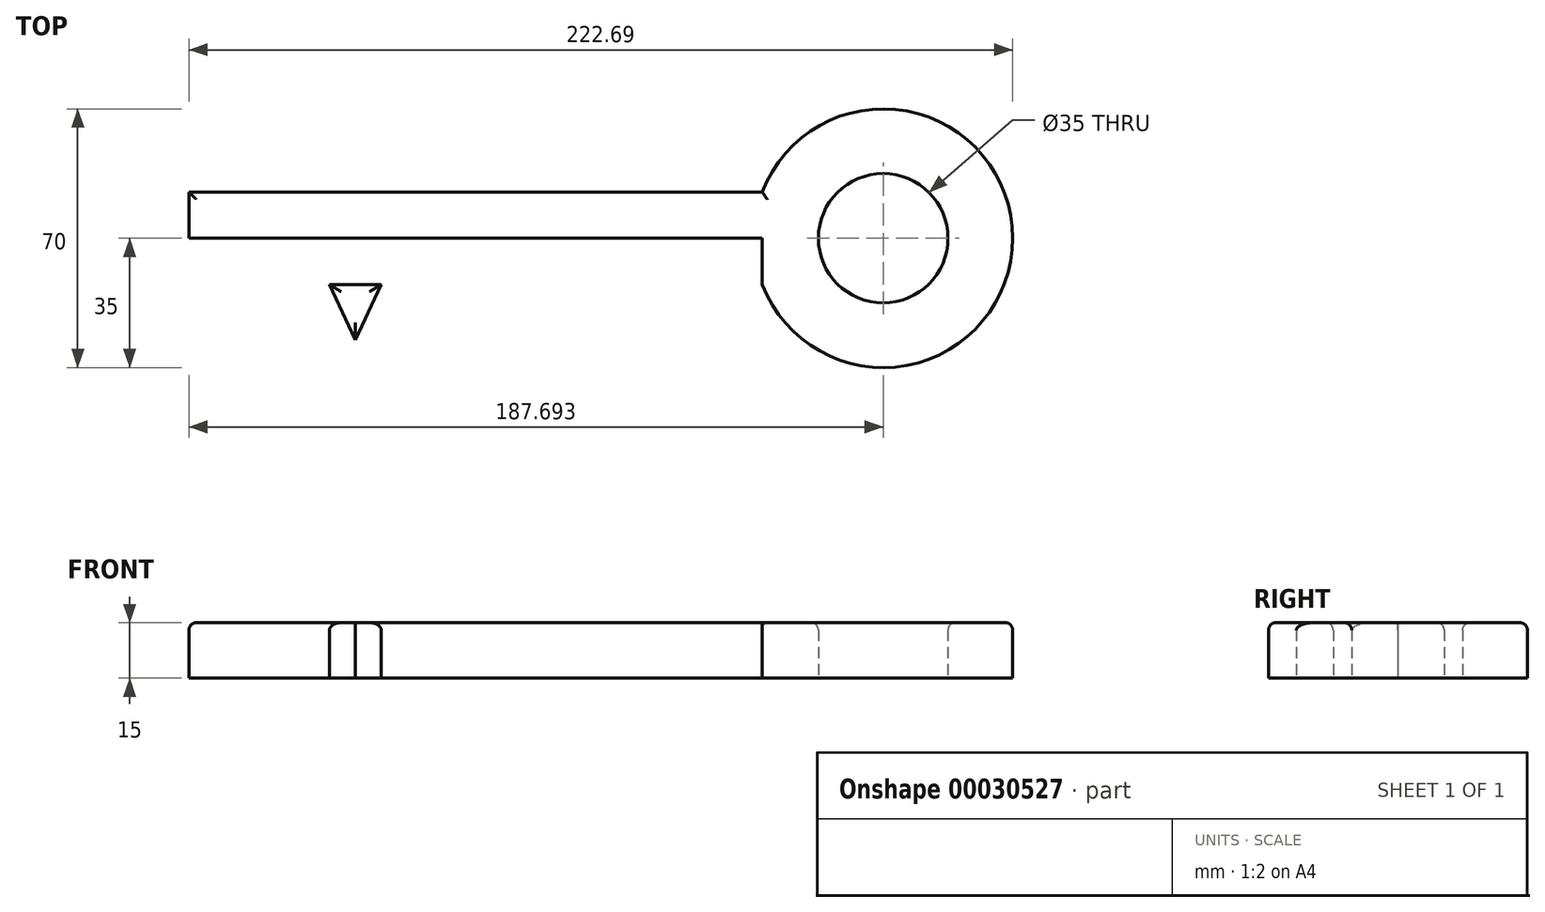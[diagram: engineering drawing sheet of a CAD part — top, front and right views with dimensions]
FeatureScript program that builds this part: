
annotation { "Feature Type Name" : "Feature", "Feature Type Description" : "" }
export const myFeature = defineFeature(function(context is Context, id is Id, definition is map)
    precondition{}
    {
        {
            var Q0;
            Q0=qCreatedBy(makeId("Top.planeOp"),FACE);
            var sketch = newSketch(context, id + "F0", { "sketchPlane" : qUnion([Q0])});
            skLineSegment(sketch, "E0.bottom", {"start": v(-137.39, 40) * mm, "end": v(17.61, 40) * mm});
            skLineSegment(sketch, "E0.top", {"start": v(-137.39, 15) * mm, "end": v(17.61, 15) * mm});
            skLineSegment(sketch, "E0.left", {"start": v(-137.39, 40) * mm, "end": v(-137.39, 15) * mm});
            skLineSegment(sketch, "E0.right", {"start": v(17.61, 40) * mm, "end": v(17.61, 15) * mm});
            skLineSegment(sketch, "E1.bottom", {"start": v(-137.39, 15) * mm, "end": v(-127.39, 15) * mm});
            skLineSegment(sketch, "E1.top", {"start": v(-137.39, -15) * mm, "end": v(-127.39, -15) * mm});
            skLineSegment(sketch, "E1.left", {"start": v(-137.39, 15) * mm, "end": v(-137.39, -15) * mm});
            skLineSegment(sketch, "E1.right", {"start": v(-127.39, 15) * mm, "end": v(-127.39, -15) * mm});
            skLineSegment(sketch, "E2.bottom", {"start": v(-117.39, 15) * mm, "end": v(-109.39, 15) * mm});
            skLineSegment(sketch, "E2.top", {"start": v(-117.39, 0) * mm, "end": v(-109.39, 0) * mm});
            skLineSegment(sketch, "E2.left", {"start": v(-117.39, 15) * mm, "end": v(-117.39, 0) * mm});
            skLineSegment(sketch, "E2.right", {"start": v(-109.39, 15) * mm, "end": v(-109.39, 0) * mm});
            skArc(sketch, "E3", {"start": v(17.61, 15) * mm, "mid": v(85.3, 27.5) * mm, "end": v(17.61, 40) * mm});
            skLineSegment(sketch, "E4", {"start": v(-137.39, 27.5) * mm, "end": v(50.3, 27.5) * mm});
            skLineSegment(sketch, "E5", {"start": v(-99.39, 15) * mm, "end": v(-92.39, 0) * mm});
            skLineSegment(sketch, "E6", {"start": v(-92.39, 0) * mm, "end": v(-85.39, 15) * mm});
            skLineSegment(sketch, "E7", {"start": v(-85.39, 15) * mm, "end": v(-99.39, 15) * mm});
            skCircle(sketch, "E8", {"center": v(50.3, 27.5) * mm, "radius": 17.5 * mm});
            skSolve(sketch);
        }
        {
            var Q0;
            {var subQ5=sQuery(id+"F0.wireOp",EDGE,"E0.bottom");Q0=makeQuery(id+"F0.imprint","IMPRINT",FACE,{"disambiguationData":[TD([[makeQuery(id+"F0.imprint","IMPRINT",EDGE,{"derivedFrom":subQ5}),-1.0]])]});}
            var Q1;
            {var subQ6=sQuery(id+"F0.wireOp",EDGE,"E1.bottom");Q1=makeQuery(id+"F0.imprint","IMPRINT",FACE,{"disambiguationData":[TD([[makeQuery(id+"F0.imprint","IMPRINT",EDGE,{"derivedFrom":subQ6}),1.0]])]});}
            var Q2;
            {var subQ0=sQuery(id+"F0.wireOp",EDGE,"E3");Q2=makeQuery(id+"F0.imprint","IMPRINT",FACE,{"disambiguationData":[TD([[makeQuery(id+"F0.imprint","IMPRINT",EDGE,{"derivedFrom":subQ0}),1.0]])]});}
            var Q3;
            Q3=makeQuery(id+"F0.imprint","IMPRINT",FACE,{"disambiguationData":[TD([[makeQuery(id+"F0.imprint","IMPRINT",EDGE,{"derivedFrom":sQuery(id+"F0.wireOp",EDGE,"E5")}),1.0]])]});
            var Q4;
            Q4=makeQuery(id+"F0.imprint","IMPRINT",FACE,{"disambiguationData":[TD([[makeQuery(id+"F0.imprint","IMPRINT",EDGE,{"derivedFrom":sQuery(id+"F0.wireOp",EDGE,"E2.bottom")}),-1.0]])]});
            var Q5;
            Q5=makeQuery(id+"F0.imprint","IMPRINT",FACE,{"disambiguationData":[TD([[makeQuery(id+"F0.imprint","IMPRINT",EDGE,{"derivedFrom":sQuery(id+"F0.wireOp",EDGE,"E1.bottom")}),-1.0]])]});
            extrude(context, id + "F1", {"entities" : qUnion([Q0, Q1, Q2, Q3, Q4, Q5]), "depth" : 15 * mm});
        }
        {
            var Q0;
            Q0=makeQuery(id+"F1.opExtrude","CAP_EDGE",EDGE,{"disambiguationData":[OSD([sQuery(id+"F0.wireOp",EDGE,"E0.bottom")])],"isStart":false});
            var Q1;
            Q1=makeQuery(id+"F1.opExtrude","CAP_EDGE",EDGE,{"disambiguationData":[OSD([sQuery(id+"F0.wireOp",EDGE,"E3")])],"isStart":false});
            var Q2;
            {var subQ0=sQuery(id+"F0.wireOp",EDGE,"E0.top");Q2=makeQuery(id+"F1.opExtrude","CAP_EDGE",EDGE,{"disambiguationData":[OSD([subQ0]),TDD([makeQuery(id+"F0.imprint","IMPRINT",EDGE,{"disambiguationData":[TD([[makeQuery(id+"F0.imprint","INTERSECT",VERTEX,{"derivedFrom":[subQ0,sQuery(id+"F0.wireOp",EDGE,"E0.right"),sQuery(id+"F0.wireOp",EDGE,"E3")]}),1.0]])],"derivedFrom":subQ0})])],"isStart":false});}
            var Q3;
            Q3=makeQuery(id+"F1.opExtrude","CAP_EDGE",EDGE,{"disambiguationData":[OSD([sQuery(id+"F0.wireOp",EDGE,"E6")])],"isStart":false});
            var Q4;
            {var subQ0=sQuery(id+"F0.wireOp",EDGE,"E0.top");Q4=makeQuery(id+"F1.opExtrude","CAP_EDGE",EDGE,{"disambiguationData":[OSD([subQ0]),TDD([makeQuery(id+"F0.imprint","IMPRINT",EDGE,{"disambiguationData":[TD([[makeQuery(id+"F0.imprint","INTERSECT",VERTEX,{"derivedFrom":[subQ0,sQuery(id+"F0.wireOp",EDGE,"E2.bottom"),sQuery(id+"F0.wireOp",EDGE,"E2.right")]}),-1.0]])],"derivedFrom":subQ0})])],"isStart":false});}
            var Q5;
            Q5=makeQuery(id+"F1.opExtrude","CAP_EDGE",EDGE,{"disambiguationData":[OSD([sQuery(id+"F0.wireOp",EDGE,"E2.right")])],"isStart":false});
            var Q6;
            {var subQ0=sQuery(id+"F0.wireOp",EDGE,"E0.top");Q6=makeQuery(id+"F1.opExtrude","CAP_EDGE",EDGE,{"disambiguationData":[OSD([subQ0]),TDD([makeQuery(id+"F0.imprint","IMPRINT",EDGE,{"disambiguationData":[TD([[makeQuery(id+"F0.imprint","INTERSECT",VERTEX,{"derivedFrom":[subQ0,sQuery(id+"F0.wireOp",EDGE,"E1.bottom"),sQuery(id+"F0.wireOp",EDGE,"E1.right")]}),-1.0]])],"derivedFrom":subQ0})])],"isStart":false});}
            var Q7;
            Q7=makeQuery(id+"F1.opExtrude","CAP_EDGE",EDGE,{"disambiguationData":[OSD([sQuery(id+"F0.wireOp",EDGE,"E1.top")])],"isStart":false});
            var Q8;
            Q8=makeQuery(id+"F1.opExtrude","CAP_EDGE",EDGE,{"disambiguationData":[OSD([sQuery(id+"F0.wireOp",EDGE,"E1.right")])],"isStart":false});
            var Q9;
            Q9=makeQuery(id+"F1.opExtrude","CAP_EDGE",EDGE,{"disambiguationData":[OSD([sQuery(id+"F0.wireOp",EDGE,"E0.left"),sQuery(id+"F0.wireOp",EDGE,"E1.left")])],"isStart":false});
            var Q10;
            Q10=makeQuery(id+"F1.opExtrude","CAP_EDGE",EDGE,{"disambiguationData":[OSD([sQuery(id+"F0.wireOp",EDGE,"E2.top")])],"isStart":false});
            var Q11;
            Q11=makeQuery(id+"F1.opExtrude","CAP_EDGE",EDGE,{"disambiguationData":[OSD([sQuery(id+"F0.wireOp",EDGE,"E2.left")])],"isStart":false});
            var Q12;
            Q12=makeQuery(id+"F1.opExtrude","CAP_EDGE",EDGE,{"disambiguationData":[OSD([sQuery(id+"F0.wireOp",EDGE,"E5")])],"isStart":false});
            var Q13;
            Q13=makeQuery(id+"F1.opExtrude","CAP_EDGE",EDGE,{"disambiguationData":[OSD([sQuery(id+"F0.wireOp",EDGE,"E8")])],"isStart":false});
            fillet(context, id + "F2", {"entities" : qUnion([Q0, Q1, Q2, Q3, Q4, Q5, Q6, Q7, Q8, Q9, Q10, Q11, Q12, Q13]), "radius" : 2 * mm, "tangentPropagation" : true, "allowEdgeOverflow" : false});
        }
    });
